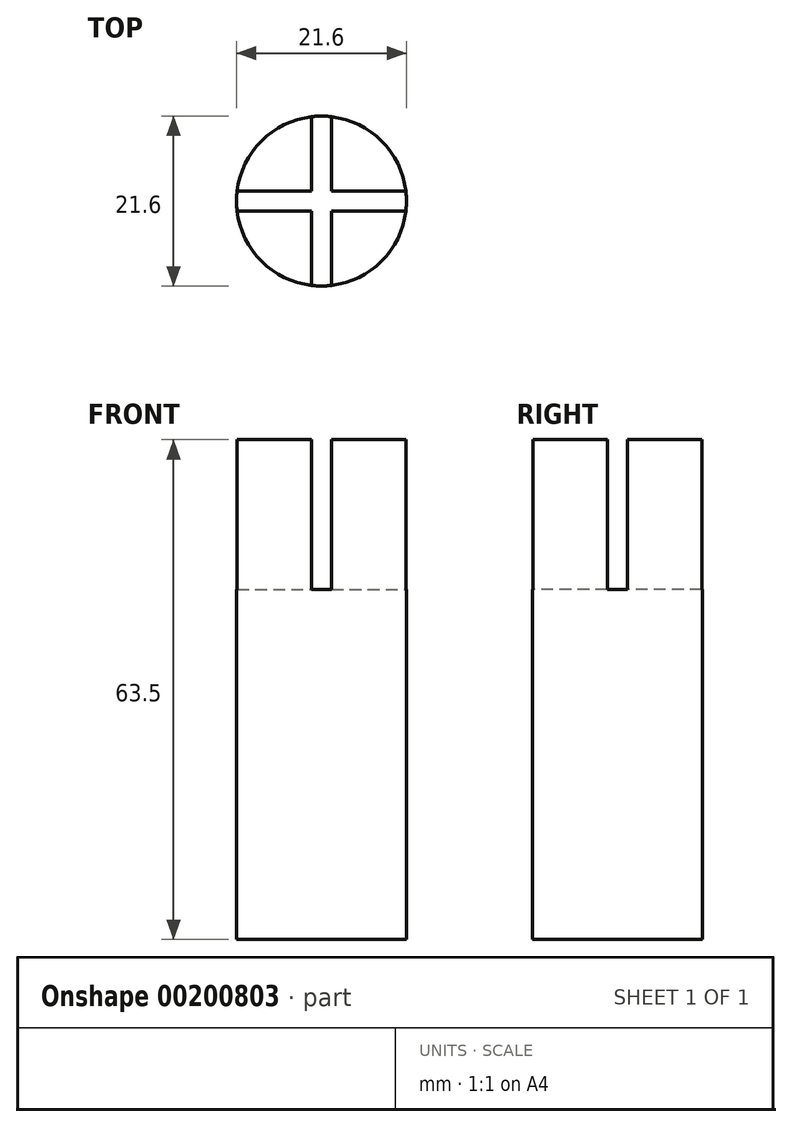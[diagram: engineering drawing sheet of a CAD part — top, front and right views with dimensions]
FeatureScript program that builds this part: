
annotation { "Feature Type Name" : "Feature", "Feature Type Description" : "" }
export const myFeature = defineFeature(function(context is Context, id is Id, definition is map)
    precondition{}
    {
        {
            var Q0;
            Q0=qCreatedBy(makeId("Top.planeOp"),FACE);
            var sketch = newSketch(context, id + "F0", { "sketchPlane" : qUnion([Q0])});
            skCircle(sketch, "E0", {"center": v(0, 0) * mm, "radius": 10.8 * mm});
            skSolve(sketch);
        }
        {
            var Q0;
            Q0=makeQuery(id+"F0.imprint","IMPRINT",FACE,{"disambiguationData":[TD([[makeQuery(id+"F0.imprint","IMPRINT",EDGE,{"derivedFrom":sQuery(id+"F0.wireOp",EDGE,"E0")}),1.0]])]});
            extrude(context, id + "F1", {"entities" : qUnion([Q0]), "depth" : 63.5 * mm});
        }
        {
            var Q0;
            Q0=makeQuery(id+"F1.opExtrude","CAP_FACE",FACE,{"disambiguationData":[OSD([sQuery(id+"F0.wireOp",EDGE,"E0")])],"isStart":false});
            var sketch = newSketch(context, id + "F2", { "sketchPlane" : qUnion([Q0])});
            skLineSegment(sketch, "E1.bottom", {"start": v(-1.27, 12.7) * mm, "end": v(1.27, 12.7) * mm});
            skLineSegment(sketch, "E1.top", {"start": v(-1.27, -12.7) * mm, "end": v(1.27, -12.7) * mm});
            skLineSegment(sketch, "E1.left", {"start": v(-1.27, 12.7) * mm, "end": v(-1.27, -12.7) * mm});
            skLineSegment(sketch, "E1.right", {"start": v(1.27, 12.7) * mm, "end": v(1.27, -12.7) * mm});
            skPoint(sketch, "E1.middle", {"position": v(0, 0) * mm});
            skLineSegment(sketch, "E2.bottom", {"start": v(-12.7, 1.27) * mm, "end": v(12.7, 1.27) * mm});
            skLineSegment(sketch, "E2.top", {"start": v(-12.7, -1.27) * mm, "end": v(12.7, -1.27) * mm});
            skLineSegment(sketch, "E2.left", {"start": v(-12.7, 1.27) * mm, "end": v(-12.7, -1.27) * mm});
            skLineSegment(sketch, "E2.right", {"start": v(12.7, 1.27) * mm, "end": v(12.7, -1.27) * mm});
            skSolve(sketch);
        }
        {
            var Q0;
            {var subQ0=sQuery(id+"F2.wireOp",EDGE,"E2.bottom");var subQ5=sQuery(id+"F2.wireOp",EDGE,"E1.left");var subQ8=makeQuery(id+"F2.imprint","INTERSECT",VERTEX,{"derivedFrom":[subQ5,subQ0]});Q0=makeQuery(id+"F2.imprint","IMPRINT",FACE,{"disambiguationData":[TD([[makeQuery(id+"F2.imprint","IMPRINT",EDGE,{"disambiguationData":[TD([[subQ8,-1.0]])],"derivedFrom":subQ5}),-1.0]])]});}
            var Q1;
            {var subQ0=sQuery(id+"F2.wireOp",EDGE,"E2.top");var subQ1=sQuery(id+"F2.wireOp",EDGE,"E1.left");var subQ2=makeQuery(id+"F2.imprint","INTERSECT",VERTEX,{"derivedFrom":[subQ1,subQ0]});Q1=makeQuery(id+"F2.imprint","IMPRINT",FACE,{"disambiguationData":[TD([[makeQuery(id+"F2.imprint","IMPRINT",EDGE,{"disambiguationData":[TD([[subQ2,-1.0]])],"derivedFrom":subQ1}),1.0]])]});}
            var Q2;
            {var subQ2=sQuery(id+"F2.wireOp",EDGE,"E1.left");var subQ4=sQuery(id+"F2.wireOp",EDGE,"E2.bottom");var subQ5=makeQuery(id+"F2.imprint","INTERSECT",VERTEX,{"derivedFrom":[subQ2,subQ4]});Q2=makeQuery(id+"F2.imprint","IMPRINT",FACE,{"disambiguationData":[TD([[makeQuery(id+"F2.imprint","IMPRINT",EDGE,{"disambiguationData":[TD([[subQ5,1.0]])],"derivedFrom":subQ2}),1.0]])]});}
            var Q3;
            {var subQ0=sQuery(id+"F2.wireOp",EDGE,"E2.bottom");var subQ5=sQuery(id+"F2.wireOp",EDGE,"E1.right");var subQ8=makeQuery(id+"F2.imprint","INTERSECT",VERTEX,{"derivedFrom":[subQ5,subQ0]});Q3=makeQuery(id+"F2.imprint","IMPRINT",FACE,{"disambiguationData":[TD([[makeQuery(id+"F2.imprint","IMPRINT",EDGE,{"disambiguationData":[TD([[subQ8,-1.0]])],"derivedFrom":subQ5}),1.0]])]});}
            var Q4;
            {var subQ0=sQuery(id+"F2.wireOp",EDGE,"E2.bottom");var subQ1=sQuery(id+"F2.wireOp",EDGE,"E1.left");var subQ2=makeQuery(id+"F2.imprint","INTERSECT",VERTEX,{"derivedFrom":[subQ1,subQ0]});Q4=makeQuery(id+"F2.imprint","IMPRINT",FACE,{"disambiguationData":[TD([[makeQuery(id+"F2.imprint","IMPRINT",EDGE,{"disambiguationData":[TD([[subQ2,-1.0]])],"derivedFrom":subQ1}),1.0]])]});}
            extrude(context, id + "F3", {"entities" : qUnion([Q0, Q1, Q2, Q3, Q4]), "operationType" : NewBodyOperationType.REMOVE, "oppositeDirection" : true, "depth" : 19.05 * mm});
        }
    });
